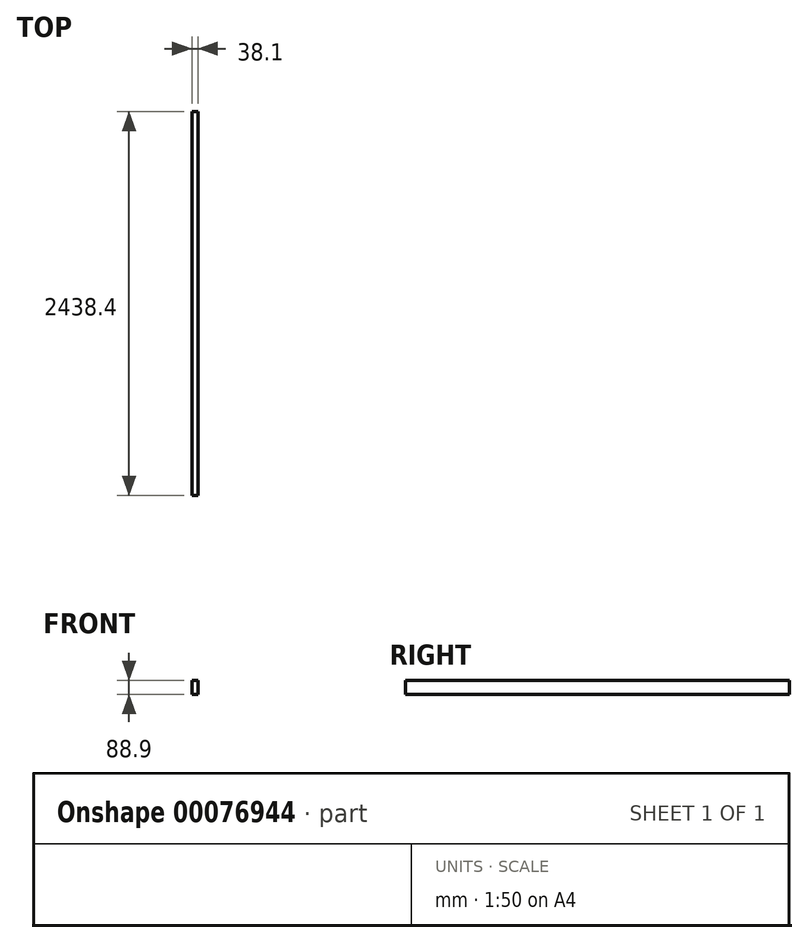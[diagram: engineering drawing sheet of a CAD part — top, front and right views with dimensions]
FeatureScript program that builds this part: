
annotation { "Feature Type Name" : "Feature", "Feature Type Description" : "" }
export const myFeature = defineFeature(function(context is Context, id is Id, definition is map)
    precondition{}
    {
        {
            var Q0;
            Q0=qCreatedBy(makeId("Front.planeOp"),FACE);
            var sketch = newSketch(context, id + "F0", { "sketchPlane" : qUnion([Q0])});
            skLineSegment(sketch, "E0.bottom", {"start": v(0, 0) * mm, "end": v(38.1, 0) * mm});
            skLineSegment(sketch, "E0.top", {"start": v(0, 88.9) * mm, "end": v(38.1, 88.9) * mm});
            skLineSegment(sketch, "E0.left", {"start": v(0, 0) * mm, "end": v(0, 88.9) * mm});
            skLineSegment(sketch, "E0.right", {"start": v(38.1, 0) * mm, "end": v(38.1, 88.9) * mm});
            skSolve(sketch);
        }
        {
            var Q0;
            Q0 = qSketchRegion(id + "F0", true);
            extrude(context, id + "F1", {"entities" : qUnion([Q0]), "depth" : 2438.4 * mm});
        }
    });
